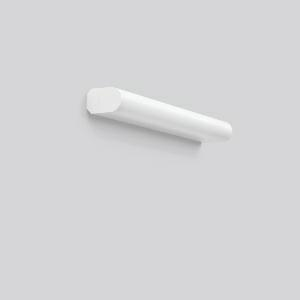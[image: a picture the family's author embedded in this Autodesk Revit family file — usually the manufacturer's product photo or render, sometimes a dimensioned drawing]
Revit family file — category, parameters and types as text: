
# Revit family: rt_44_451168_002_1_dba7
name_source: partatom
category: Lighting Fixtures
units: mm (PartAtom-declared; Revit-internal decimal feet)

## family parameters
Cut with Voids When Loaded = No
Host = Face
Light Source = No
Part Type = Normal
Room Calculation Point = No
Round Connector Dimension = Use Diameter
Shared = No

## types (1)
- RT 44 (1 x LED Modul 840, 970 lm, 4000)
    Apparent Load = 10 VA
    CIE Flux Codes = 36 64 85 81 100
    Color Rendering = 80
    Color Temperature = 4000
    Default Elevation = 1800 mm
    Description = Series: RT 44
Linear luminaire, can be used as wall and mirror luminaire. Base: aluminium, powder-coated. End caps: plastic (polycarbonate), shock-resistant. Diffuser: plastic (polycarbonate), opal. Suitable for Ceiling mounting, Wall (surface). Can be installed horizontally and vertically. Very easy installation thanks to Plug+Play connection. Driver integrated. High type of protection: IP44 for use in wet areas. 
Colour: pure white (RAL 9010)
Length: 600 mm
Width: 55 mm
Height: 87 mm
Lamp: LED
Socket: without socket
Colour temperature: 4000K
Colour rendering index (CRI): 80
System power: 10 W
Rated luminous flux: 970 lm
Luminous efficiency: 97 lm/W
Control gear: Regulated power supply
Protection class: I
Type of protection: IP 44
    Height = 87 mm
    Lamp = 1 x LED Modul 840
    Lamp Light Flux = 970 lm
    Lamp count = 1
    Length = 600 mm
    Lifetime = 50000 h
    Luminous efficacy = 97 lm/W
    Manufacturer = RZB
    ModVariant = No
    Model = 451168.002.1
    Mounting Place = Ceiling, Wall
    Mounting Type = Surface mounted
    Number of Poles = 1
    OnlyDefault = Yes
    Power Factor = 1
    Product Name = RT 44
    Product group = Surface mounted ceiling and wall luminaires
    ProductGroupID = 305
    Protection Class = Protection class I
    Protection Degree = IP 44
    RLX_Detail_Level = 1
    RLX_Emergency_Light_Flux = 0 lm
    RLX_Emergency_Type = 0
    RLX_Emergency_Type_DB = No
    RlxData = <blob elided: 24629 chars, md5=3df07d38>
    Socket = socket
    Standby Power = 0 W
    System Light Flux = 970 lm
    System Power = 10 W
    Type Comments = Product without accessories
    Type Image = 451054.752.jpg
    URL = http://relux.com
    VarID = ---
    Voltage = 230 V
    Voltage Range = 220-240 V
    Weight = 0.00 kg
    Width = 55 mm

## geometry (parser evidence)
native form markers: Blend x4, Sweep x13
no freeform markers — native parametric forms only
